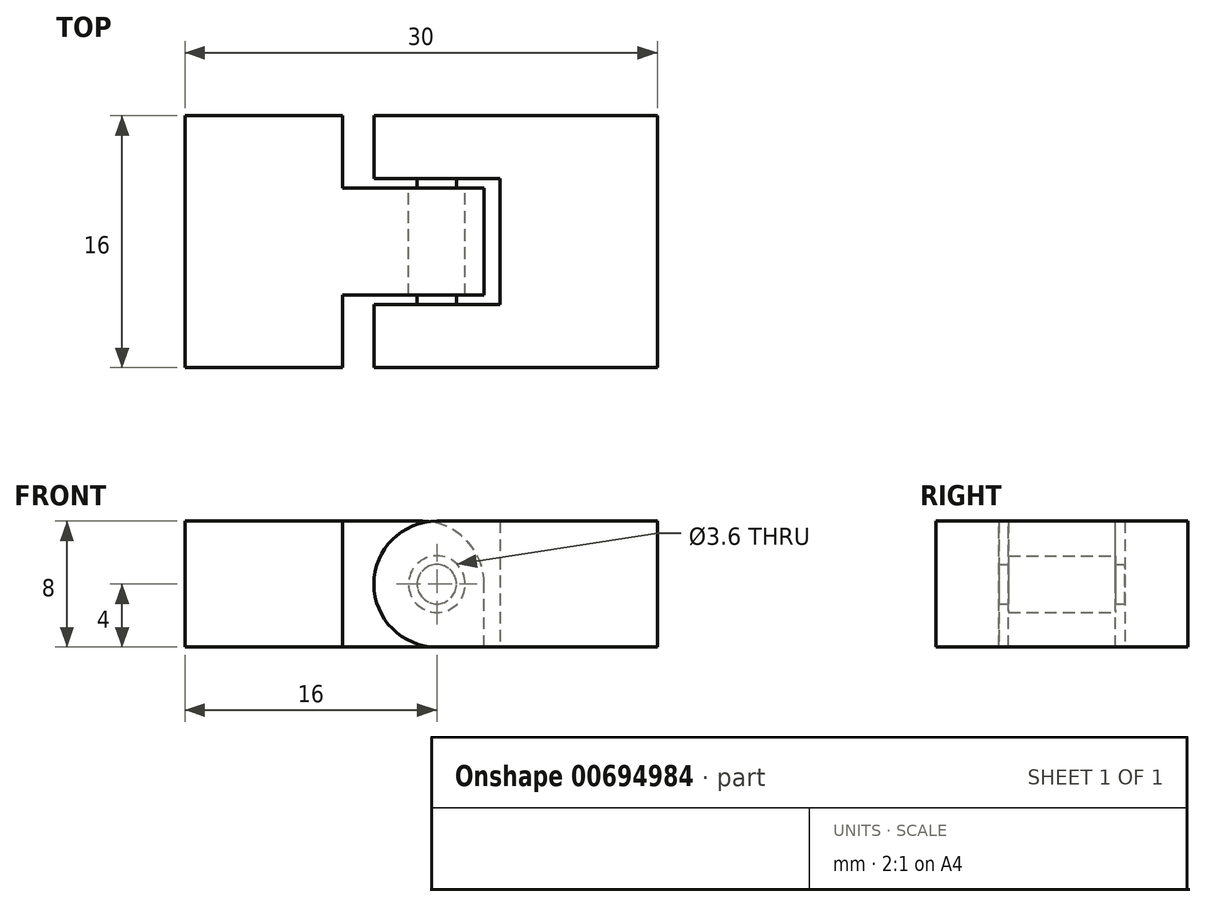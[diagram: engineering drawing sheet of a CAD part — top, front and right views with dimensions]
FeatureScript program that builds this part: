
annotation { "Feature Type Name" : "Feature", "Feature Type Description" : "" }
export const myFeature = defineFeature(function(context is Context, id is Id, definition is map)
    precondition{}
    {
        {
            var Q0;
            Q0=qCreatedBy(makeId("Top.planeOp"),FACE);
            var sketch = newSketch(context, id + "F0", { "sketchPlane" : qUnion([Q0])});
            skLineSegment(sketch, "E0", {"start": v(0, 4) * mm, "end": v(0, 8) * mm});
            skLineSegment(sketch, "E1", {"start": v(0, 8) * mm, "end": v(18, 8) * mm});
            skLineSegment(sketch, "E2", {"start": v(18, 8) * mm, "end": v(18, -8) * mm});
            skLineSegment(sketch, "E3", {"start": v(18, -8) * mm, "end": v(0, -8) * mm});
            skLineSegment(sketch, "E4", {"start": v(0, -8) * mm, "end": v(0, -4) * mm});
            skLineSegment(sketch, "E5", {"start": v(0, -4) * mm, "end": v(8, -4) * mm});
            skLineSegment(sketch, "E6", {"start": v(8, -4) * mm, "end": v(8, 4) * mm});
            skLineSegment(sketch, "E7", {"start": v(8, 4) * mm, "end": v(0, 4) * mm});
            skSolve(sketch);
        }
        {
            var Q0;
            Q0=makeQuery(id+"F0.imprint","IMPRINT",FACE,{"disambiguationData":[TD([[makeQuery(id+"F0.imprint","IMPRINT",EDGE,{"derivedFrom":sQuery(id+"F0.wireOp",EDGE,"E0")}),-1.0]])]});
            extrude(context, id + "F1", {"entities" : qUnion([Q0]), "depth" : 8 * mm, "offsetDistance" : 25 * mm});
        }
        {
            var Q0;
            Q0=makeQuery(id+"F1.opExtrude","SWEPT_FACE",FACE,{"disambiguationData":[OSD([sQuery(id+"F0.wireOp",EDGE,"E7")])]});
            var sketch = newSketch(context, id + "F2", { "sketchPlane" : qUnion([Q0])});
            skLineSegment(sketch, "E8", {"start": v(8, 0) * mm, "end": v(0, 8) * mm, "construction": true});
            skCircle(sketch, "E9", {"center": v(4, 4) * mm, "radius": 1.25 * mm});
            skSolve(sketch);
        }
        {
            var Q0;
            Q0=makeQuery(id+"F2.imprint","IMPRINT",FACE,{"disambiguationData":[TD([[makeQuery(id+"F2.imprint","IMPRINT",EDGE,{"derivedFrom":sQuery(id+"F2.wireOp",EDGE,"E9")}),1.0]])]});
            var Q1;
            Q1=makeQuery(id+"F1.opExtrude","SWEPT_FACE",FACE,{"disambiguationData":[OSD([sQuery(id+"F0.wireOp",EDGE,"E5")])]});
            extrude(context, id + "F3", {"entities" : qUnion([Q0]), "operationType" : NewBodyOperationType.ADD, "endBound" : BoundingType.UP_TO_SURFACE, "depth" : 25 * mm, "endBoundEntityFace" : qUnion([Q1]), "offsetDistance" : 25 * mm});
        }
        {
            var Q0;
            Q0=makeQuery(id+"F1.opExtrude","CAP_FACE",FACE,{"disambiguationData":[OSD([sQuery(id+"F0.wireOp",EDGE,"E0"),sQuery(id+"F0.wireOp",EDGE,"E1"),sQuery(id+"F0.wireOp",EDGE,"E2"),sQuery(id+"F0.wireOp",EDGE,"E3"),sQuery(id+"F0.wireOp",EDGE,"E4"),sQuery(id+"F0.wireOp",EDGE,"E5"),sQuery(id+"F0.wireOp",EDGE,"E6"),sQuery(id+"F0.wireOp",EDGE,"E7")])],"isStart":false});
            var sketch = newSketch(context, id + "F4", { "sketchPlane" : qUnion([Q0])});
            skLineSegment(sketch, "E10", {"start": v(7, 3.4) * mm, "end": v(7, -3.4) * mm});
            skLineSegment(sketch, "E11", {"start": v(7, -3.4) * mm, "end": v(-2, -3.4) * mm});
            skLineSegment(sketch, "E12", {"start": v(-2, -3.4) * mm, "end": v(-2, -8) * mm});
            skLineSegment(sketch, "E13", {"start": v(-2, -8) * mm, "end": v(-12, -8) * mm});
            skLineSegment(sketch, "E14", {"start": v(-12, -8) * mm, "end": v(-12, 8) * mm});
            skLineSegment(sketch, "E15", {"start": v(-12, 8) * mm, "end": v(-2, 8) * mm});
            skLineSegment(sketch, "E16", {"start": v(-2, 8) * mm, "end": v(-2, 3.4) * mm});
            skLineSegment(sketch, "E17", {"start": v(-2, 3.4) * mm, "end": v(7, 3.4) * mm});
            skSolve(sketch);
        }
        {
            var Q0;
            Q0=makeQuery(id+"F4.imprint","IMPRINT",FACE,{"disambiguationData":[TD([[makeQuery(id+"F4.imprint","IMPRINT",EDGE,{"derivedFrom":sQuery(id+"F4.wireOp",EDGE,"E10")}),-1.0]])]});
            var Q1;
            Q1=makeQuery(id+"F1.opExtrude","CAP_FACE",FACE,{"disambiguationData":[OSD([sQuery(id+"F0.wireOp",EDGE,"E0"),sQuery(id+"F0.wireOp",EDGE,"E1"),sQuery(id+"F0.wireOp",EDGE,"E2"),sQuery(id+"F0.wireOp",EDGE,"E3"),sQuery(id+"F0.wireOp",EDGE,"E4"),sQuery(id+"F0.wireOp",EDGE,"E5"),sQuery(id+"F0.wireOp",EDGE,"E6"),sQuery(id+"F0.wireOp",EDGE,"E7")])],"isStart":true});
            extrude(context, id + "F5", {"entities" : qUnion([Q0]), "endBound" : BoundingType.UP_TO_SURFACE, "oppositeDirection" : true, "depth" : 25 * mm, "endBoundEntityFace" : qUnion([Q1]), "offsetDistance" : 25 * mm});
        }
        {
            var Q0;
            Q0=makeQuery(id+"F5.opExtrude","SWEPT_FACE",FACE,{"disambiguationData":[OSD([sQuery(id+"F4.wireOp",EDGE,"E17")])]});
            var sketch = newSketch(context, id + "F6", { "sketchPlane" : qUnion([Q0])});
            skCircle(sketch, "E18.0", {"center": v(-4, 4) * mm, "radius": 1.25 * mm, "construction": true});
            skCircle(sketch, "E19", {"center": v(-4, 4) * mm, "radius": 1.8 * mm});
            skSolve(sketch);
        }
        {
            var Q0;
            Q0=makeQuery(id+"F6.imprint","IMPRINT",FACE,{"disambiguationData":[TD([[makeQuery(id+"F6.imprint","IMPRINT",EDGE,{"derivedFrom":sQuery(id+"F6.wireOp",EDGE,"E19")}),1.0]])]});
            var Q1;
            Q1=sQuery(id+"F6.wireOp",EDGE,"E18.0");
            var Q2;
            Q2=makeQuery(id+"F5.opExtrude","SWEPT_FACE",FACE,{"disambiguationData":[OSD([sQuery(id+"F4.wireOp",EDGE,"E11")])]});
            extrude(context, id + "F7", {"entities" : qUnion([Q0]), "operationType" : NewBodyOperationType.REMOVE, "surfaceEntities" : qUnion([Q1]), "endBound" : BoundingType.UP_TO_SURFACE, "oppositeDirection" : true, "depth" : 25 * mm, "endBoundEntityFace" : qUnion([Q2]), "offsetDistance" : 25 * mm});
        }
        {
            var Q0;
            Q0=makeQuery(id+"F5.opExtrude","CAP_EDGE",EDGE,{"disambiguationData":[OSD([sQuery(id+"F4.wireOp",EDGE,"E10")])],"isStart":true});
            var Q1;
            Q1=makeQuery(id+"F5.opExtrude","TWEAK_EDGE",EDGE,{"derivedFrom":[makeQuery(id+"F1.opExtrude","CAP_FACE",FACE,{"disambiguationData":[OSD([sQuery(id+"F0.wireOp",EDGE,"E0"),sQuery(id+"F0.wireOp",EDGE,"E1"),sQuery(id+"F0.wireOp",EDGE,"E2"),sQuery(id+"F0.wireOp",EDGE,"E3"),sQuery(id+"F0.wireOp",EDGE,"E4"),sQuery(id+"F0.wireOp",EDGE,"E5"),sQuery(id+"F0.wireOp",EDGE,"E6"),sQuery(id+"F0.wireOp",EDGE,"E7")])],"isStart":true}),makeQuery(id+"F4.imprint","IMPRINT",EDGE,{"derivedFrom":sQuery(id+"F4.wireOp",EDGE,"E10")})]});
            var Q2;
            Q2=makeQuery(id+"F1.opExtrude","CAP_EDGE",EDGE,{"disambiguationData":[OSD([sQuery(id+"F0.wireOp",EDGE,"E0")])],"isStart":false});
            var Q3;
            Q3=makeQuery(id+"F1.opExtrude","CAP_EDGE",EDGE,{"disambiguationData":[OSD([sQuery(id+"F0.wireOp",EDGE,"E4")])],"isStart":false});
            var Q4;
            Q4=makeQuery(id+"F1.opExtrude","CAP_EDGE",EDGE,{"disambiguationData":[OSD([sQuery(id+"F0.wireOp",EDGE,"E4")])],"isStart":true});
            var Q5;
            Q5=makeQuery(id+"F1.opExtrude","CAP_EDGE",EDGE,{"disambiguationData":[OSD([sQuery(id+"F0.wireOp",EDGE,"E0")])],"isStart":true});
            fillet(context, id + "F8", {"entities" : qUnion([Q0, Q1, Q2, Q3, Q4, Q5]), "radius" : 4 * mm, "tangentPropagation" : true, "allowEdgeOverflow" : false});
        }
    });
